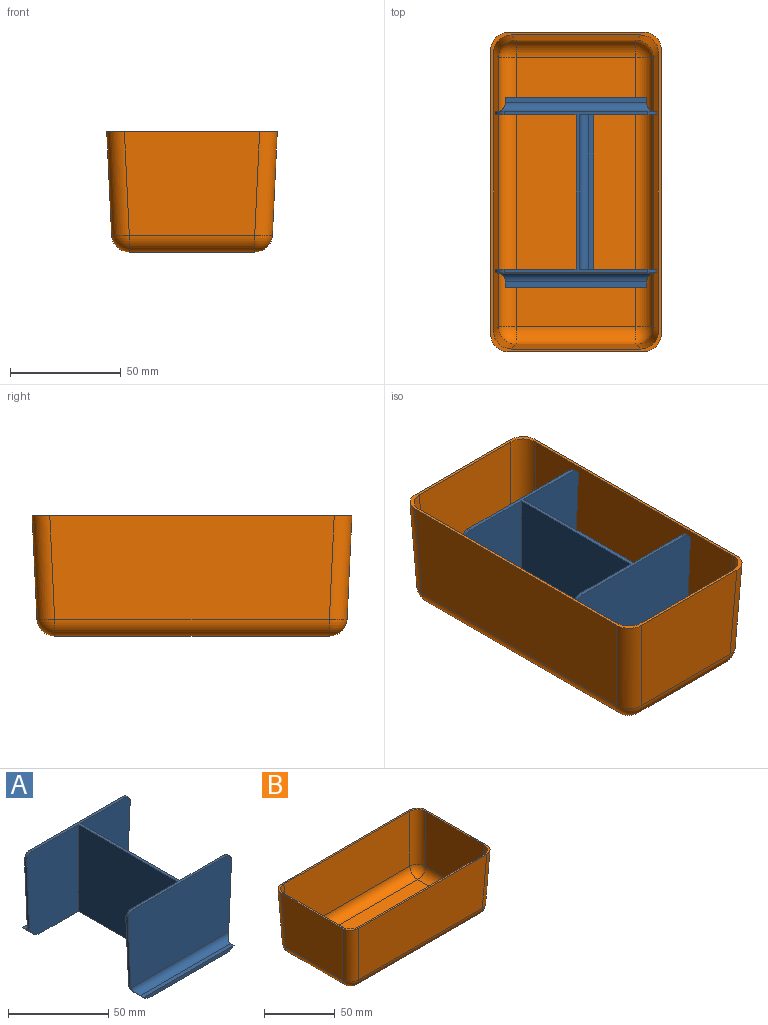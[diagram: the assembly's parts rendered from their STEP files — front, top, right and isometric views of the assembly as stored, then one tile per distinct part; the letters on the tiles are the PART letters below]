
ASSEMBLY  parts=2 mates=1
PART A: 31 faces, bbox 73.1x86x53 mm
  f0: plane 86x53.24mm, normal (0,0,-1), area 1411.8mm2, adj f1,f5,f6,f7,f10,f13,f14,f17
  f1: plane 70x2mm, normal (1,0,0), area 140mm2, adj f0,f2,f10,f13
  f2: plane 70x2.4mm, normal (0,0,1), area 168mm2, adj f1,f10,f13,f26
  f3: plane 70x47mm, normal (1,0,0), area 3290mm2, adj f4,f10,f13,f26
  f4: plane 73.2x65.11mm, normal (0,0,1), area 320.4mm2, adj f3,f5,f6,f9,f10,f13,f14,f15
  f5: plane 70x53mm, normal (-1,0,0), area 3710mm2, adj f0,f4,f6,f14
  f6: plane 53x36.56mm, normal (0,-1,0), area 1865.4mm2, adj f0,f4,f5,f12,f22,f29
  f7: plane 63.82x2mm, normal (0,1,0), area 121mm2, adj f0,f8,f22,f23
  f8: plane 63.82x2.4mm, normal (0,0,1), area 153.2mm2, adj f7,f22,f23,f24
  f9: plane 73.11x47mm, normal (0,1,0), area 3342.5mm2, adj f4,f11,f12,f22,f23,f24,f29,f30
  f10: plane 53x34.96mm, normal (0,-1,0), area 1764.4mm2, adj f0,f1,f2,f3,f4,f11,f23,f26
  f11: plane 41.19x1.94mm, normal (1,0,-0.05), area 66mm2, adj f9,f10,f23,f30
  f12: plane 41.19x1.94mm, normal (-1,0,-0.05), area 66mm2, adj f6,f9,f22,f29
  f13: plane 53x34.96mm, normal (0,1,0), area 1764.4mm2, adj f0,f1,f2,f3,f4,f18,f21,f26
  f14: plane 53x36.56mm, normal (0,1,0), area 1865.4mm2, adj f0,f4,f5,f19,f20,f27
  f15: plane 73.11x47mm, normal (0,-1,0), area 3342.5mm2, adj f4,f18,f19,f20,f21,f25,f27,f28
  f16: plane 63.82x2.4mm, normal (0,0,1), area 153.2mm2, adj f17,f20,f21,f25
  f17: plane 63.82x2mm, normal (0,-1,0), area 121mm2, adj f0,f16,f20,f21
  f18: plane 41.19x1.94mm, normal (1,0,-0.05), area 66mm2, adj f13,f15,f21,f28
  f19: plane 41.19x1.94mm, normal (-1,0,-0.05), area 66mm2, adj f14,f15,f20,f27
  f20: cylinder r=8mm len=8mm, axis (0,1,0), area 61.1mm2, adj f0,f14,f15,f16,f17,f19,f25
  f21: cylinder r=8mm len=8mm, axis (0,1,0), area 61.1mm2, adj f0,f13,f15,f16,f17,f18,f25
  f22: cylinder r=8mm len=8mm, axis (0,1,0), area 61.1mm2, adj f0,f6,f7,f8,f9,f12,f24
  f23: cylinder r=8mm len=8mm, axis (0,1,0), area 61.1mm2, adj f0,f7,f8,f9,f10,f11,f24
  f24: cylinder r=4mm len=68.73mm, axis (-1,0,0), area 415.1mm2, adj f8,f9,f22,f23
  f25: cylinder r=4mm len=68.73mm, axis (1,0,0), area 415.1mm2, adj f15,f16,f20,f21
  f26: cylinder r=4mm len=70mm, axis (0,1,0), area 439.8mm2, adj f2,f3,f10,f13
  f27: cylinder r=4mm len=4.19mm, axis (0,-1,0), area 10.4mm2, adj f4,f14,f15,f19
  f28: cylinder r=4mm len=4.19mm, axis (0,-1,0), area 10.4mm2, adj f4,f13,f15,f18
  f29: cylinder r=4mm len=4.19mm, axis (0,-1,0), area 10.4mm2, adj f4,f6,f9,f12
  f30: cylinder r=4mm len=4.19mm, axis (0,-1,0), area 10.4mm2, adj f4,f9,f10,f11
PART B: 35 faces, bbox 144.6x77.1x54.5 mm
  f0: plane 61.12x46.68mm, normal (1,0,-0.05), area 2753.1mm2, adj f8,f13,f16,f26
  f1: plane 128.62x46.68mm, normal (0,1,-0.05), area 5907.3mm2, adj f8,f13,f14,f22
  f2: plane 61.12x46.68mm, normal (-1,0,-0.05), area 2753.1mm2, adj f8,f14,f15,f19
  f3: plane 58.52x45.38mm, normal (1,0,0.05), area 2561.1mm2, adj f8,f9,f12,f32
  f4: plane 126.02x45.38mm, normal (0,-1,0.05), area 5627.4mm2, adj f8,f9,f10,f28
  f5: plane 58.52x45.38mm, normal (-1,0,0.05), area 2561.1mm2, adj f8,f10,f11,f29
  f6: plane 126.02x45.38mm, normal (0,1,0.05), area 5627.4mm2, adj f8,f11,f12,f33
  f7: plane 128.62x46.68mm, normal (0,-1,-0.05), area 5907.3mm2, adj f8,f15,f16,f23
  f8: plane 144.6x77.1mm, normal (0,0,1), area 569.7mm2, adj f0,f1,f2,f3,f4,f5,f6,f7
  f9: cylinder r=8mm len=45.69mm, axis (0.05,-0.05,-1), area 572mm2, adj f3,f4,f8,f30
  f10: cylinder r=8mm len=45.69mm, axis (-0.05,-0.05,-1), area 572mm2, adj f4,f5,f8,f27
  f11: cylinder r=8mm len=45.69mm, axis (-0.05,0.05,-1), area 572mm2, adj f5,f6,f8,f31
  f12: cylinder r=8mm len=45.69mm, axis (0.05,0.05,-1), area 572mm2, adj f3,f6,f8,f34
  f13: cylinder r=8mm len=46.99mm, axis (0.05,0.05,1), area 588.3mm2, adj f0,f1,f8,f24
  f14: cylinder r=8mm len=46.99mm, axis (-0.05,0.05,1), area 588.3mm2, adj f1,f2,f8,f20
  f15: cylinder r=8mm len=46.99mm, axis (-0.05,-0.05,1), area 588.3mm2, adj f2,f7,f8,f21
  f16: cylinder r=8mm len=46.99mm, axis (0.05,-0.05,1), area 588.3mm2, adj f0,f7,f8,f25
  f17: plane 121.74x54.24mm, normal (0,0,1), area 6602.8mm2, adj f28,f29,f32,f33
  f18: plane 124.22x56.72mm, normal (0,0,-1), area 7044.9mm2, adj f19,f22,f23,f26
  f19: cylinder r=8mm len=56.72mm, axis (0,1,0), area 691.3mm2, adj f2,f18,f20,f21
  f20: sphere r=8mm, area 94.5mm2, adj f14,f19,f22
  f21: sphere r=8mm, area 94.5mm2, adj f15,f19,f23
  f22: cylinder r=8mm len=124.22mm, axis (1,0,0), area 1514.1mm2, adj f1,f18,f20,f24
  f23: cylinder r=8mm len=124.22mm, axis (1,0,0), area 1514.1mm2, adj f7,f18,f21,f25
  f24: sphere r=8mm, area 94.5mm2, adj f13,f22,f26
  f25: sphere r=8mm, area 94.5mm2, adj f16,f23,f26
  f26: cylinder r=8mm len=56.72mm, axis (0,-1,0), area 691.3mm2, adj f0,f18,f24,f25
  f27: sphere r=8mm, area 94.5mm2, adj f10,f28,f29
  f28: cylinder r=8mm len=121.74mm, axis (-1,0,0), area 1483.9mm2, adj f4,f17,f27,f30
  f29: cylinder r=8mm len=54.24mm, axis (0,-1,0), area 661.1mm2, adj f5,f17,f27,f31
  f30: sphere r=8mm, area 94.5mm2, adj f9,f28,f32
  f31: sphere r=8mm, area 94.5mm2, adj f11,f29,f33
  f32: cylinder r=8mm len=54.24mm, axis (0,-1,0), area 661.1mm2, adj f3,f17,f30,f34
  f33: cylinder r=8mm len=121.74mm, axis (-1,0,0), area 1483.9mm2, adj f6,f17,f31,f34
  f34: sphere r=8mm, area 94.5mm2, adj f12,f32,f33
PLACE A t=(-33.12,-31.53,17.42)mm
PLACE B rot(axis=(0,0,1),90deg) t=(-33.12,-31.53,17.42)mm
MATE revolute A.f0 <-> B.f17  axis (0,0,1) through (-33.12,-31.53,17.42)mm
